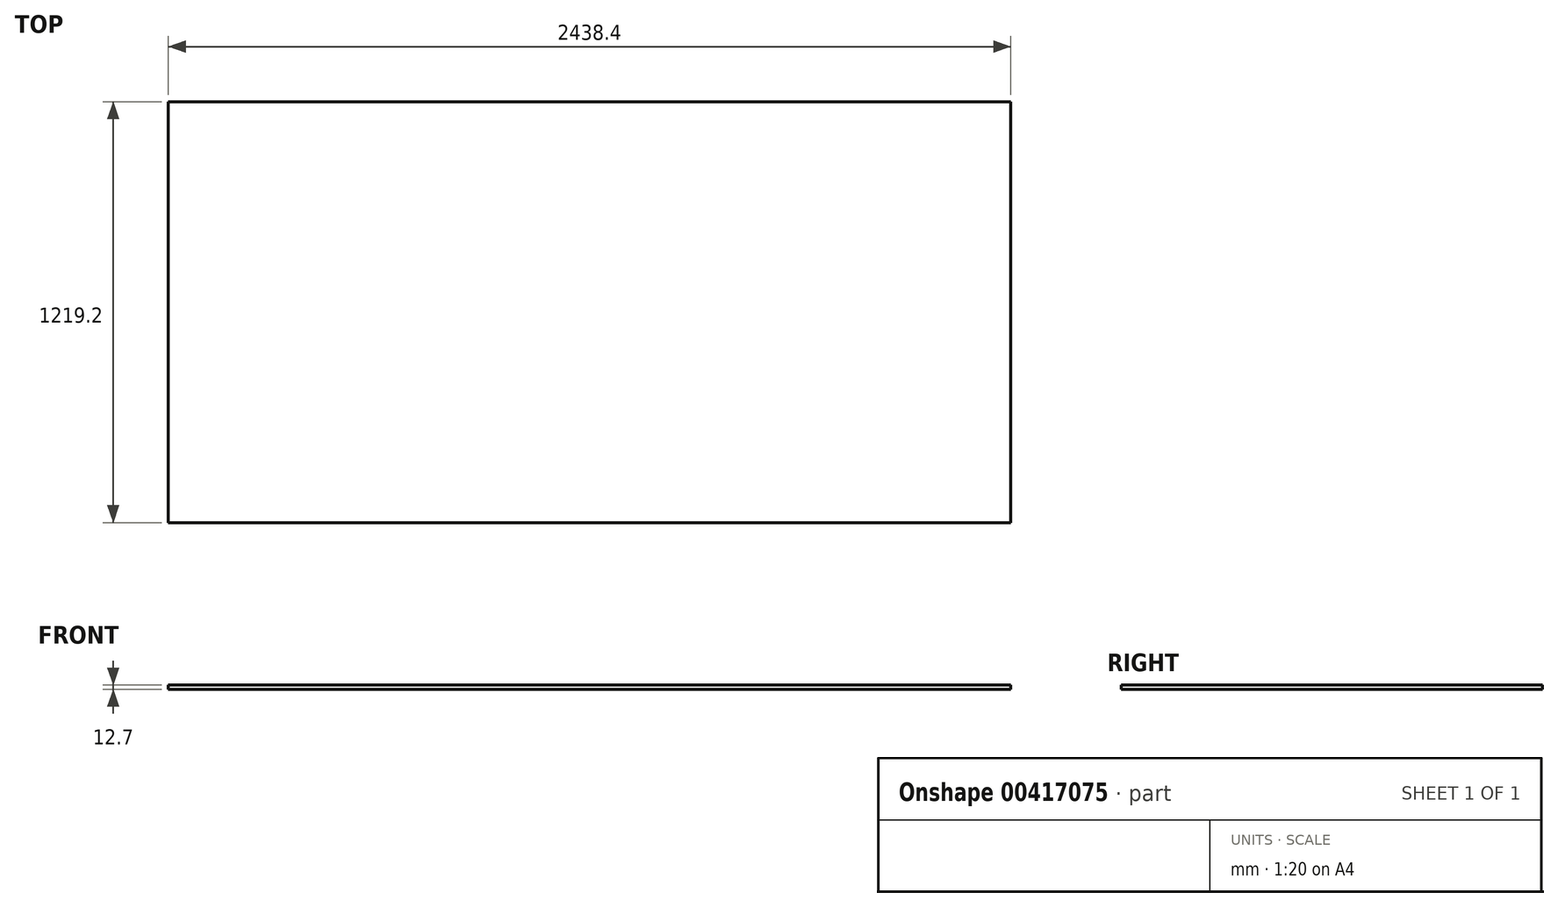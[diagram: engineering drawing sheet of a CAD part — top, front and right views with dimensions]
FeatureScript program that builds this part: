
annotation { "Feature Type Name" : "Feature", "Feature Type Description" : "" }
export const myFeature = defineFeature(function(context is Context, id is Id, definition is map)
    precondition{}
    {
        {
            var Q0;
            Q0=qCreatedBy(makeId("Top.planeOp"),FACE);
            var sketch = newSketch(context, id + "F0", { "sketchPlane" : qUnion([Q0])});
            skLineSegment(sketch, "E0.bottom", {"start": v(1219.2, 609.6) * mm, "end": v(-1219.2, 609.6) * mm});
            skLineSegment(sketch, "E0.top", {"start": v(1219.2, -609.6) * mm, "end": v(-1219.2, -609.6) * mm});
            skLineSegment(sketch, "E0.left", {"start": v(1219.2, 609.6) * mm, "end": v(1219.2, -609.6) * mm});
            skLineSegment(sketch, "E0.right", {"start": v(-1219.2, 609.6) * mm, "end": v(-1219.2, -609.6) * mm});
            skPoint(sketch, "E0.middle", {"position": v(0, 0) * mm});
            skSolve(sketch);
        }
        {
            var Q0;
            Q0 = qSketchRegion(id + "F0", true);
            extrude(context, id + "F1", {"entities" : qUnion([Q0]), "depth" : 12.7 * mm});
        }
    });
